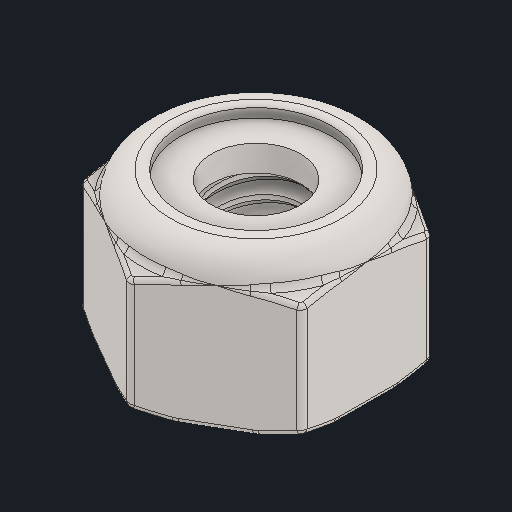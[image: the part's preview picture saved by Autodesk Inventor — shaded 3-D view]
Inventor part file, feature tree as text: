
AUTODESK INVENTOR PART (.ipt)
format: ipt  version: 2024 (Build 280153000, 153)  size: 522,240 bytes
history: native  units: in
note: dims shown in document units (in); Inventor stores cm internally (conversion verified against a paired STEP export)
features: fillet x1
ambient origin geometry x8: Origin, YZ Plane, XZ Plane, XY Plane, X Axis, Y Axis, Z Axis, Center Point
bodies: Solid1 (feature_tree)
feature tree (1):
  fillet  "Fillet4"  [1 undecoded]
note: 1 required parameter value undecoded (feature->parameter linkage not recoverable at this tier; creation-order binding heuristic only, values carry confidence <= 0.55)
